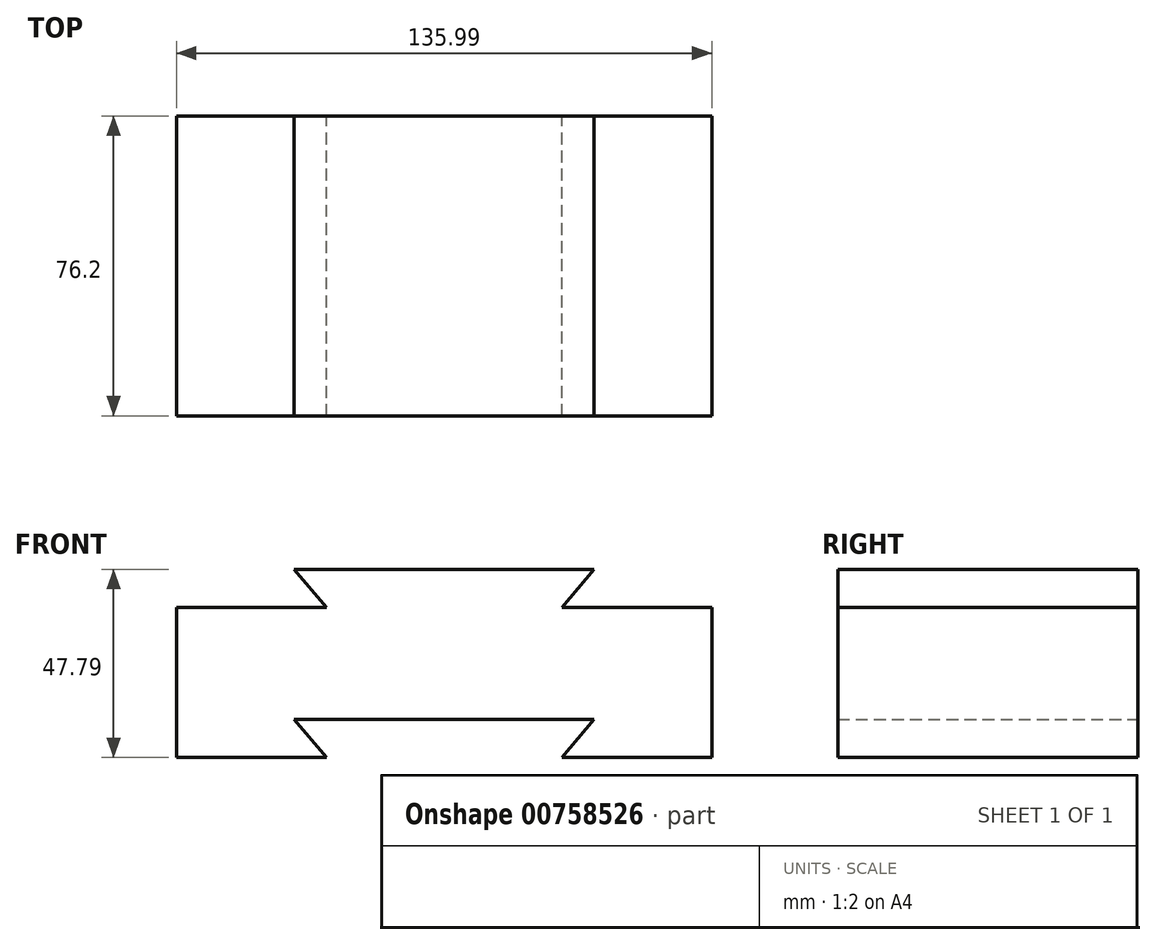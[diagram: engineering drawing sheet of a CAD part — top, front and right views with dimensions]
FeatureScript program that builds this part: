
annotation { "Feature Type Name" : "Feature", "Feature Type Description" : "" }
export const myFeature = defineFeature(function(context is Context, id is Id, definition is map)
    precondition{}
    {
        {
            var Q0;
            Q0=qCreatedBy(makeId("Front.planeOp"),FACE);
            var sketch = newSketch(context, id + "F0", { "sketchPlane" : qUnion([Q0])});
            skLineSegment(sketch, "E0", {"start": v(10.48, -38.1) * mm, "end": v(48.58, -38.1) * mm});
            skLineSegment(sketch, "E1", {"start": v(10.48, -38.1) * mm, "end": v(18.68, -28.4) * mm});
            skLineSegment(sketch, "E2", {"start": v(48.58, -38.1) * mm, "end": v(48.58, 0) * mm});
            skLineSegment(sketch, "E3", {"start": v(48.58, 0) * mm, "end": v(10.48, 0) * mm});
            skLineSegment(sketch, "E4", {"start": v(10.48, 0) * mm, "end": v(18.68, 9.7) * mm});
            skLineSegment(sketch, "E5", {"start": v(18.68, 9.7) * mm, "end": v(-57.52, 9.7) * mm});
            skLineSegment(sketch, "E6", {"start": v(-57.52, 9.7) * mm, "end": v(-49.31, 0) * mm});
            skLineSegment(sketch, "E7", {"start": v(-49.31, 0) * mm, "end": v(-87.41, 0) * mm});
            skLineSegment(sketch, "E8", {"start": v(-87.41, 0) * mm, "end": v(-87.41, -38.1) * mm});
            skLineSegment(sketch, "E9", {"start": v(-87.41, -38.1) * mm, "end": v(-49.31, -38.1) * mm});
            skLineSegment(sketch, "E10", {"start": v(-49.31, -38.1) * mm, "end": v(-57.52, -28.4) * mm});
            skLineSegment(sketch, "E11", {"start": v(-57.52, -28.4) * mm, "end": v(18.68, -28.4) * mm});
            skSolve(sketch);
        }
        {
            var Q0;
            Q0 = qSketchRegion(id + "F0", true);
            extrude(context, id + "F1", {"entities" : qUnion([Q0]), "depth" : 76.2 * mm, "offsetDistance" : 25.4 * mm});
        }
    });
